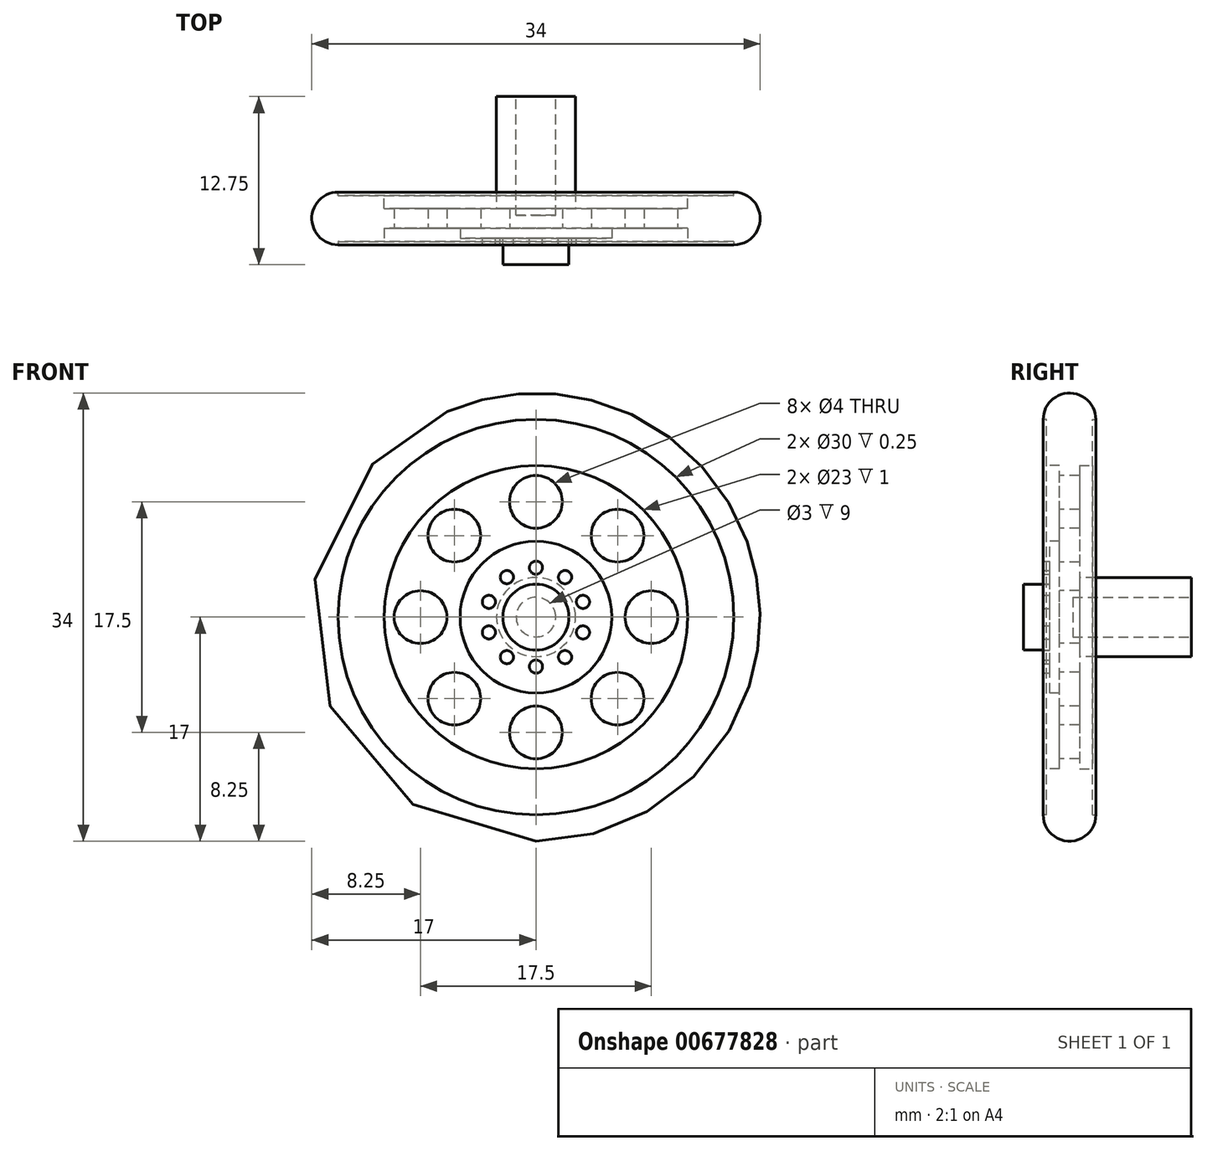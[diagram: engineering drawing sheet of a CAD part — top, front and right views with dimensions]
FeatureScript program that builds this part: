
annotation { "Feature Type Name" : "Feature", "Feature Type Description" : "" }
export const myFeature = defineFeature(function(context is Context, id is Id, definition is map)
    precondition{}
    {
        {
            var Q0;
            Q0=qCreatedBy(makeId("Front.planeOp"),FACE);
            var sketch = newSketch(context, id + "F0", { "sketchPlane" : qUnion([Q0])});
            skCircle(sketch, "E0", {"center": v(0, 0) * mm, "radius": 17 * mm});
            skSolve(sketch);
        }
        {
            var Q0;
            Q0=makeQuery(id+"F0.imprint","IMPRINT",FACE,{"disambiguationData":[TD([[makeQuery(id+"F0.imprint","IMPRINT",EDGE,{"derivedFrom":sQuery(id+"F0.wireOp",EDGE,"E0")}),1.0]])]});
            extrude(context, id + "F1", {"entities" : qUnion([Q0]), "depth" : 4 * mm, "offsetDistance" : 25 * mm});
        }
        {
            var Q0;
            Q0=makeQuery(id+"F1.opExtrude","CAP_FACE",FACE,{"disambiguationData":[OSD([sQuery(id+"F0.wireOp",EDGE,"E0")])],"isStart":false});
            fillet(context, id + "F2", {"entities" : qUnion([Q0]), "radius" : 2 * mm, "tangentPropagation" : true, "allowEdgeOverflow" : false});
        }
        {
            var Q0;
            Q0=makeQuery(id+"F1.opExtrude","CAP_FACE",FACE,{"disambiguationData":[OSD([sQuery(id+"F0.wireOp",EDGE,"E0")])],"isStart":true});
            fillet(context, id + "F3", {"entities" : qUnion([Q0]), "radius" : 2 * mm, "tangentPropagation" : true, "allowEdgeOverflow" : false});
        }
        {
            var Q0;
            Q0=makeQuery(id+"F1.opExtrude","CAP_FACE",FACE,{"disambiguationData":[OSD([sQuery(id+"F0.wireOp",EDGE,"E0")])],"isStart":false});
            var sketch = newSketch(context, id + "F4", { "sketchPlane" : qUnion([Q0])});
            skCircle(sketch, "E1", {"center": v(0, 0) * mm, "radius": 5.75 * mm});
            skCircle(sketch, "E2", {"center": v(0, 8.75) * mm, "radius": 2 * mm});
            skCircle(sketch, "E3.1.0", {"center": v(-6.19, 6.19) * mm, "radius": 2 * mm});
            skCircle(sketch, "E3.2.0", {"center": v(-8.75, 0) * mm, "radius": 2 * mm});
            skCircle(sketch, "E3.3.0", {"center": v(-6.19, -6.19) * mm, "radius": 2 * mm});
            skCircle(sketch, "E3.4.0", {"center": v(0, -8.75) * mm, "radius": 2 * mm});
            skCircle(sketch, "E3.5.0", {"center": v(6.19, -6.19) * mm, "radius": 2 * mm});
            skCircle(sketch, "E3.6.0", {"center": v(8.75, 0) * mm, "radius": 2 * mm});
            skCircle(sketch, "E3.7.0", {"center": v(6.19, 6.19) * mm, "radius": 2 * mm});
            skSolve(sketch);
        }
        {
            var Q0;
            Q0=makeQuery(id+"F4.imprint","IMPRINT",FACE,{"disambiguationData":[TD([[makeQuery(id+"F4.imprint","IMPRINT",EDGE,{"derivedFrom":sQuery(id+"F4.wireOp",EDGE,"E1")}),-1.0]])]});
            extrude(context, id + "F5", {"entities" : qUnion([Q0]), "operationType" : NewBodyOperationType.REMOVE, "oppositeDirection" : true, "depth" : 0.25 * mm, "offsetDistance" : 25 * mm});
        }
        {
            var Q0;
            Q0=makeQuery(id+"F1.opExtrude","CAP_FACE",FACE,{"disambiguationData":[OSD([sQuery(id+"F0.wireOp",EDGE,"E0")])],"isStart":true});
            extrude(context, id + "F6", {"entities" : qUnion([Q0]), "operationType" : NewBodyOperationType.REMOVE, "oppositeDirection" : true, "depth" : .25 * mm, "offsetDistance" : 25 * mm});
        }
        {
            var Q0;
            Q0=makeQuery(id+"F5.boolean.opBoolean","COPY",FACE,{"derivedFrom":makeQuery(id+"F5.opExtrude","CAP_FACE",FACE,{"disambiguationData":[OSD([sQuery(id+"F0.wireOp",EDGE,"E0"),sQuery(id+"F4.wireOp",EDGE,"E1"),sQuery(id+"F4.wireOp",EDGE,"E2"),sQuery(id+"F4.wireOp",EDGE,"E3.1.0"),sQuery(id+"F4.wireOp",EDGE,"E3.2.0"),sQuery(id+"F4.wireOp",EDGE,"E3.3.0"),sQuery(id+"F4.wireOp",EDGE,"E3.4.0"),sQuery(id+"F4.wireOp",EDGE,"E3.5.0"),sQuery(id+"F4.wireOp",EDGE,"E3.6.0"),sQuery(id+"F4.wireOp",EDGE,"E3.7.0")])],"isStart":false})});
            var sketch = newSketch(context, id + "F7", { "sketchPlane" : qUnion([Q0])});
            skCircle(sketch, "E4", {"center": v(0, 0) * mm, "radius": 11.5 * mm});
            skSolve(sketch);
        }
        {
            var Q0;
            Q0=makeQuery(id+"F7.imprint","IMPRINT",FACE,{"disambiguationData":[TD([[makeQuery(id+"F7.imprint","IMPRINT",EDGE,{"derivedFrom":sQuery(id+"F7.wireOp",EDGE,"E4")}),1.0]])]});
            extrude(context, id + "F8", {"entities" : qUnion([Q0]), "operationType" : NewBodyOperationType.REMOVE, "oppositeDirection" : true, "depth" : 1 * mm, "offsetDistance" : 25 * mm});
        }
        {
            var Q0;
            Q0=makeQuery(id+"F6.boolean.opBoolean","COPY",FACE,{"derivedFrom":makeQuery(id+"F6.opExtrude","CAP_FACE",FACE,{"disambiguationData":[OSD([sQuery(id+"F0.wireOp",EDGE,"E0")])],"isStart":false})});
            var sketch = newSketch(context, id + "F9", { "sketchPlane" : qUnion([Q0])});
            skCircle(sketch, "E5", {"center": v(0, 0) * mm, "radius": 11.5 * mm});
            skSolve(sketch);
        }
        {
            var Q0;
            Q0=makeQuery(id+"F9.imprint","IMPRINT",FACE,{"disambiguationData":[TD([[makeQuery(id+"F9.imprint","IMPRINT",EDGE,{"derivedFrom":sQuery(id+"F9.wireOp",EDGE,"E5")}),1.0]])]});
            extrude(context, id + "F10", {"entities" : qUnion([Q0]), "operationType" : NewBodyOperationType.REMOVE, "oppositeDirection" : true, "depth" : 1 * mm, "offsetDistance" : 25 * mm});
        }
        {
            var Q0;
            Q0=makeQuery(id+"F5.boolean.opBoolean","SPLIT",FACE,{"disambiguationData":[TD([makeQuery(id+"F5.opExtrude","SWEPT_FACE",FACE,{"disambiguationData":[OSD([sQuery(id+"F4.wireOp",EDGE,"E3.1.0")])]})])],"derivedFrom":makeQuery(id+"F1.opExtrude","CAP_FACE",FACE,{"disambiguationData":[OSD([sQuery(id+"F0.wireOp",EDGE,"E0")])],"isStart":false})});
            var Q1;
            Q1=makeQuery(id+"F5.boolean.opBoolean","SPLIT",FACE,{"disambiguationData":[TD([makeQuery(id+"F5.opExtrude","SWEPT_FACE",FACE,{"disambiguationData":[OSD([sQuery(id+"F4.wireOp",EDGE,"E2")])]})])],"derivedFrom":makeQuery(id+"F1.opExtrude","CAP_FACE",FACE,{"disambiguationData":[OSD([sQuery(id+"F0.wireOp",EDGE,"E0")])],"isStart":false})});
            var Q2;
            Q2=makeQuery(id+"F5.boolean.opBoolean","SPLIT",FACE,{"disambiguationData":[TD([makeQuery(id+"F5.opExtrude","SWEPT_FACE",FACE,{"disambiguationData":[OSD([sQuery(id+"F4.wireOp",EDGE,"E3.7.0")])]})])],"derivedFrom":makeQuery(id+"F1.opExtrude","CAP_FACE",FACE,{"disambiguationData":[OSD([sQuery(id+"F0.wireOp",EDGE,"E0")])],"isStart":false})});
            var Q3;
            Q3=makeQuery(id+"F5.boolean.opBoolean","SPLIT",FACE,{"disambiguationData":[TD([makeQuery(id+"F5.opExtrude","SWEPT_FACE",FACE,{"disambiguationData":[OSD([sQuery(id+"F4.wireOp",EDGE,"E3.6.0")])]})])],"derivedFrom":makeQuery(id+"F1.opExtrude","CAP_FACE",FACE,{"disambiguationData":[OSD([sQuery(id+"F0.wireOp",EDGE,"E0")])],"isStart":false})});
            var Q4;
            Q4=makeQuery(id+"F5.boolean.opBoolean","SPLIT",FACE,{"disambiguationData":[TD([makeQuery(id+"F5.opExtrude","SWEPT_FACE",FACE,{"disambiguationData":[OSD([sQuery(id+"F4.wireOp",EDGE,"E3.5.0")])]})])],"derivedFrom":makeQuery(id+"F1.opExtrude","CAP_FACE",FACE,{"disambiguationData":[OSD([sQuery(id+"F0.wireOp",EDGE,"E0")])],"isStart":false})});
            var Q5;
            Q5=makeQuery(id+"F5.boolean.opBoolean","SPLIT",FACE,{"disambiguationData":[TD([makeQuery(id+"F5.opExtrude","SWEPT_FACE",FACE,{"disambiguationData":[OSD([sQuery(id+"F4.wireOp",EDGE,"E3.4.0")])]})])],"derivedFrom":makeQuery(id+"F1.opExtrude","CAP_FACE",FACE,{"disambiguationData":[OSD([sQuery(id+"F0.wireOp",EDGE,"E0")])],"isStart":false})});
            var Q6;
            Q6=makeQuery(id+"F5.boolean.opBoolean","SPLIT",FACE,{"disambiguationData":[TD([makeQuery(id+"F5.opExtrude","SWEPT_FACE",FACE,{"disambiguationData":[OSD([sQuery(id+"F4.wireOp",EDGE,"E3.3.0")])]})])],"derivedFrom":makeQuery(id+"F1.opExtrude","CAP_FACE",FACE,{"disambiguationData":[OSD([sQuery(id+"F0.wireOp",EDGE,"E0")])],"isStart":false})});
            var Q7;
            Q7=makeQuery(id+"F5.boolean.opBoolean","SPLIT",FACE,{"disambiguationData":[TD([makeQuery(id+"F5.opExtrude","SWEPT_FACE",FACE,{"disambiguationData":[OSD([sQuery(id+"F4.wireOp",EDGE,"E3.2.0")])]})])],"derivedFrom":makeQuery(id+"F1.opExtrude","CAP_FACE",FACE,{"disambiguationData":[OSD([sQuery(id+"F0.wireOp",EDGE,"E0")])],"isStart":false})});
            extrude(context, id + "F11", {"entities" : qUnion([Q0, Q1, Q2, Q3, Q4, Q5, Q6, Q7]), "operationType" : NewBodyOperationType.REMOVE, "oppositeDirection" : true, "depth" : 5 * mm, "offsetDistance" : 25 * mm});
        }
        {
            var Q0;
            Q0=makeQuery(id+"F5.boolean.opBoolean","SPLIT",FACE,{"disambiguationData":[TD([makeQuery(id+"F5.opExtrude","SWEPT_FACE",FACE,{"disambiguationData":[OSD([sQuery(id+"F4.wireOp",EDGE,"E1")])]})])],"derivedFrom":makeQuery(id+"F1.opExtrude","CAP_FACE",FACE,{"disambiguationData":[OSD([sQuery(id+"F0.wireOp",EDGE,"E0")])],"isStart":false})});
            extrude(context, id + "F12", {"entities" : qUnion([Q0]), "operationType" : NewBodyOperationType.REMOVE, "oppositeDirection" : true, "depth" : .5 * mm, "offsetDistance" : 25 * mm});
        }
        {
            var Q0;
            Q0=makeQuery(id+"F12.boolean.opBoolean","COPY",FACE,{"derivedFrom":makeQuery(id+"F12.opExtrude","CAP_FACE",FACE,{"disambiguationData":[OSD([sQuery(id+"F0.wireOp",EDGE,"E0")])],"isStart":false})});
            var sketch = newSketch(context, id + "F13", { "sketchPlane" : qUnion([Q0])});
            skCircle(sketch, "E6", {"center": v(0, 0) * mm, "radius": 2.5 * mm});
            skCircle(sketch, "E7", {"center": v(0, 3.75) * mm, "radius": 0.5 * mm});
            skCircle(sketch, "E8.1.0", {"center": v(-2.2, 3.03) * mm, "radius": 0.5 * mm});
            skCircle(sketch, "E8.2.0", {"center": v(-3.57, 1.16) * mm, "radius": 0.5 * mm});
            skCircle(sketch, "E8.3.0", {"center": v(-3.57, -1.16) * mm, "radius": 0.5 * mm});
            skCircle(sketch, "E8.4.0", {"center": v(-2.2, -3.03) * mm, "radius": 0.5 * mm});
            skCircle(sketch, "E8.5.0", {"center": v(0, -3.75) * mm, "radius": 0.5 * mm});
            skCircle(sketch, "E8.6.0", {"center": v(2.2, -3.03) * mm, "radius": 0.5 * mm});
            skCircle(sketch, "E8.7.0", {"center": v(3.57, -1.16) * mm, "radius": 0.5 * mm});
            skCircle(sketch, "E8.8.0", {"center": v(3.57, 1.16) * mm, "radius": 0.5 * mm});
            skCircle(sketch, "E8.9.0", {"center": v(2.2, 3.03) * mm, "radius": 0.5 * mm});
            skSolve(sketch);
        }
        {
            var Q0;
            Q0=makeQuery(id+"F13.imprint","IMPRINT",FACE,{"disambiguationData":[TD([[makeQuery(id+"F13.imprint","IMPRINT",EDGE,{"derivedFrom":sQuery(id+"F13.wireOp",EDGE,"E7")}),1.0]])]});
            var Q1;
            Q1=makeQuery(id+"F13.imprint","IMPRINT",FACE,{"disambiguationData":[TD([[makeQuery(id+"F13.imprint","IMPRINT",EDGE,{"derivedFrom":sQuery(id+"F13.wireOp",EDGE,"E8.9.0")}),1.0]])]});
            var Q2;
            Q2=makeQuery(id+"F13.imprint","IMPRINT",FACE,{"disambiguationData":[TD([[makeQuery(id+"F13.imprint","IMPRINT",EDGE,{"derivedFrom":sQuery(id+"F13.wireOp",EDGE,"E8.8.0")}),1.0]])]});
            var Q3;
            Q3=makeQuery(id+"F13.imprint","IMPRINT",FACE,{"disambiguationData":[TD([[makeQuery(id+"F13.imprint","IMPRINT",EDGE,{"derivedFrom":sQuery(id+"F13.wireOp",EDGE,"E8.7.0")}),1.0]])]});
            var Q4;
            Q4=makeQuery(id+"F13.imprint","IMPRINT",FACE,{"disambiguationData":[TD([[makeQuery(id+"F13.imprint","IMPRINT",EDGE,{"derivedFrom":sQuery(id+"F13.wireOp",EDGE,"E8.6.0")}),1.0]])]});
            var Q5;
            Q5=makeQuery(id+"F13.imprint","IMPRINT",FACE,{"disambiguationData":[TD([[makeQuery(id+"F13.imprint","IMPRINT",EDGE,{"derivedFrom":sQuery(id+"F13.wireOp",EDGE,"E8.5.0")}),1.0]])]});
            var Q6;
            Q6=makeQuery(id+"F13.imprint","IMPRINT",FACE,{"disambiguationData":[TD([[makeQuery(id+"F13.imprint","IMPRINT",EDGE,{"derivedFrom":sQuery(id+"F13.wireOp",EDGE,"E8.4.0")}),1.0]])]});
            var Q7;
            Q7=makeQuery(id+"F13.imprint","IMPRINT",FACE,{"disambiguationData":[TD([[makeQuery(id+"F13.imprint","IMPRINT",EDGE,{"derivedFrom":sQuery(id+"F13.wireOp",EDGE,"E8.3.0")}),1.0]])]});
            var Q8;
            Q8=makeQuery(id+"F13.imprint","IMPRINT",FACE,{"disambiguationData":[TD([[makeQuery(id+"F13.imprint","IMPRINT",EDGE,{"derivedFrom":sQuery(id+"F13.wireOp",EDGE,"E8.2.0")}),1.0]])]});
            var Q9;
            Q9=makeQuery(id+"F13.imprint","IMPRINT",FACE,{"disambiguationData":[TD([[makeQuery(id+"F13.imprint","IMPRINT",EDGE,{"derivedFrom":sQuery(id+"F13.wireOp",EDGE,"E8.1.0")}),1.0]])]});
            extrude(context, id + "F14", {"entities" : qUnion([Q0, Q1, Q2, Q3, Q4, Q5, Q6, Q7, Q8, Q9]), "operationType" : NewBodyOperationType.ADD, "depth" : .5 * mm, "offsetDistance" : 25 * mm});
        }
        {
            var Q0;
            Q0=makeQuery(id+"F13.imprint","IMPRINT",FACE,{"disambiguationData":[TD([[makeQuery(id+"F13.imprint","IMPRINT",EDGE,{"derivedFrom":sQuery(id+"F13.wireOp",EDGE,"E6")}),1.0]])]});
            extrude(context, id + "F15", {"entities" : qUnion([Q0]), "operationType" : NewBodyOperationType.ADD, "depth" : 2 * mm, "offsetDistance" : 25 * mm});
        }
        {
            var Q0;
            Q0=makeQuery(id+"F10.boolean.opBoolean","COPY",FACE,{"derivedFrom":makeQuery(id+"F10.opExtrude","CAP_FACE",FACE,{"disambiguationData":[OSD([sQuery(id+"F9.wireOp",EDGE,"E5")])],"isStart":false})});
            var sketch = newSketch(context, id + "F16", { "sketchPlane" : qUnion([Q0])});
            skCircle(sketch, "E9", {"center": v(0, 0) * mm, "radius": 3 * mm});
            skSolve(sketch);
        }
        {
            var Q0;
            Q0=makeQuery(id+"F16.imprint","IMPRINT",FACE,{"disambiguationData":[TD([[makeQuery(id+"F16.imprint","IMPRINT",EDGE,{"derivedFrom":sQuery(id+"F16.wireOp",EDGE,"E9")}),1.0]])]});
            extrude(context, id + "F17", {"entities" : qUnion([Q0]), "operationType" : NewBodyOperationType.ADD, "depth" : 8.5 * mm, "offsetDistance" : 25 * mm});
        }
        {
            var Q0;
            Q0=makeQuery(id+"F17.opExtrude","CAP_FACE",FACE,{"disambiguationData":[OSD([sQuery(id+"F16.wireOp",EDGE,"E9")])],"isStart":false});
            var sketch = newSketch(context, id + "F18", { "sketchPlane" : qUnion([Q0])});
            skCircle(sketch, "E10", {"center": v(0, 0) * mm, "radius": 1.5 * mm});
            skSolve(sketch);
        }
        {
            var Q0;
            Q0=makeQuery(id+"F18.imprint","IMPRINT",FACE,{"disambiguationData":[TD([[makeQuery(id+"F18.imprint","IMPRINT",EDGE,{"derivedFrom":sQuery(id+"F18.wireOp",EDGE,"E10")}),1.0]])]});
            extrude(context, id + "F19", {"entities" : qUnion([Q0]), "operationType" : NewBodyOperationType.REMOVE, "oppositeDirection" : true, "depth" : 9 * mm, "offsetDistance" : 25 * mm});
        }
    });
